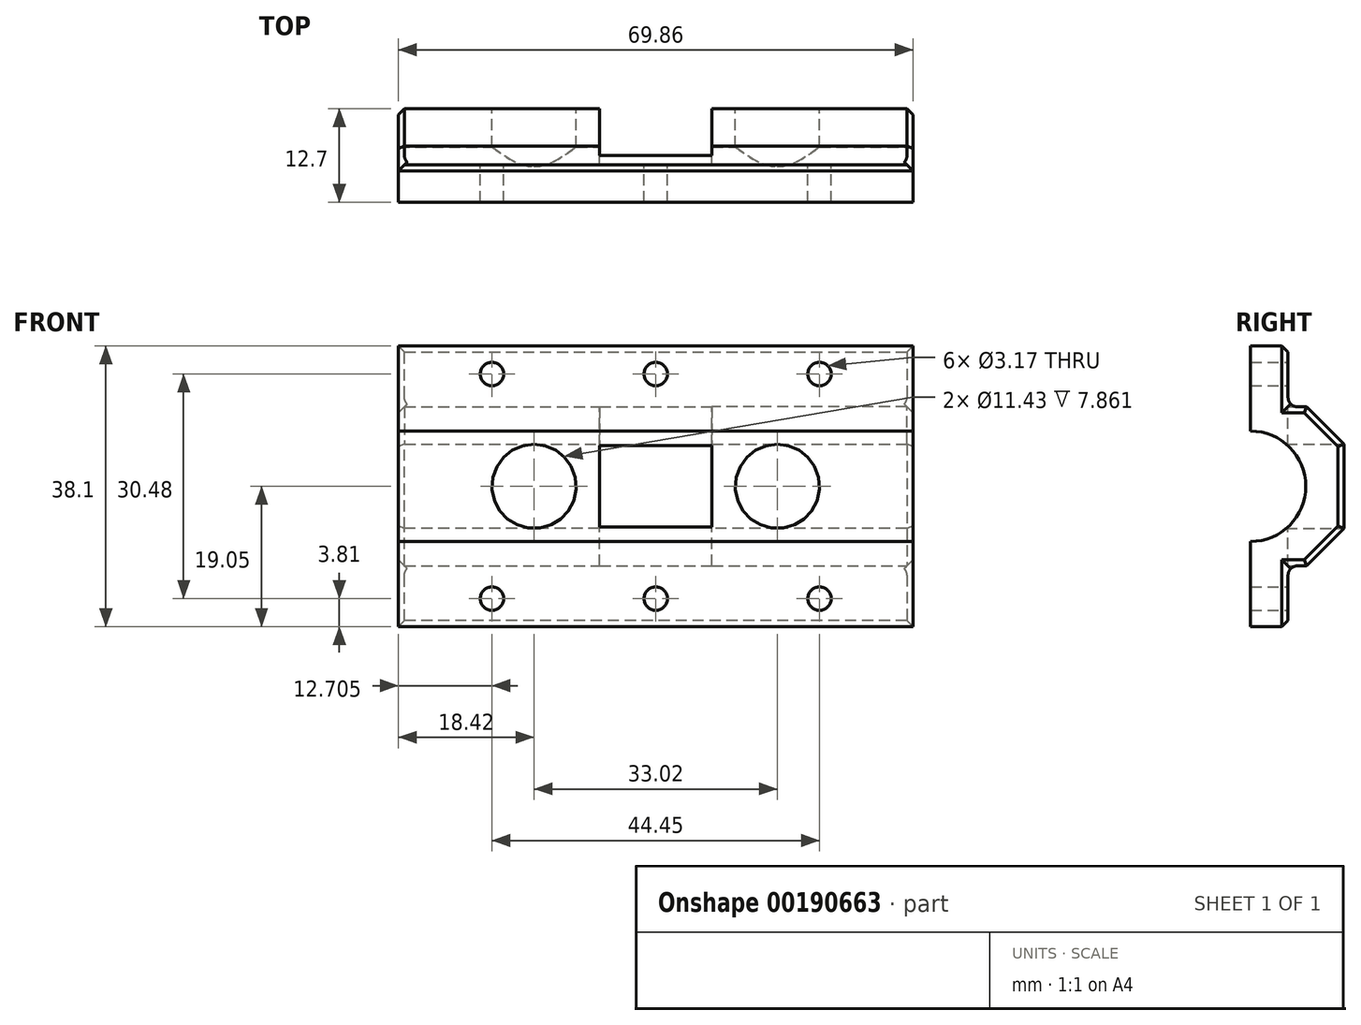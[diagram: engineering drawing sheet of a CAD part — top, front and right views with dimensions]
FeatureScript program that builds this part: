
annotation { "Feature Type Name" : "Feature", "Feature Type Description" : "" }
export const myFeature = defineFeature(function(context is Context, id is Id, definition is map)
    precondition{}
    {
        {
            var Q0;
            Q0=qCreatedBy(makeId("Top.planeOp"),FACE);
            var sketch = newSketch(context, id + "F0", { "sketchPlane" : qUnion([Q0])});
            skLineSegment(sketch, "E0", {"start": v(0, 0) * mm, "end": v(-34.93, 0) * mm});
            skLineSegment(sketch, "E1", {"start": v(-34.93, 0) * mm, "end": v(-34.93, 12.7) * mm});
            skLineSegment(sketch, "E2", {"start": v(-34.93, 12.7) * mm, "end": v(0, 12.7) * mm});
            skLineSegment(sketch, "E3", {"start": v(0, 12.7) * mm, "end": v(0, 0) * mm});
            skLineSegment(sketch, "E4.MirrorCS", {"start": v(34.93, 12.7) * mm, "end": v(0, 12.7) * mm});
            skLineSegment(sketch, "E5.MirrorCS", {"start": v(0, 0) * mm, "end": v(34.93, 0) * mm});
            skLineSegment(sketch, "E6.MirrorCS", {"start": v(34.93, 0) * mm, "end": v(34.93, 12.7) * mm});
            skSolve(sketch);
        }
        {
            var Q0;
            Q0=qSketchRegion(id+"F0",true);
            extrude(context, id + "F1", {"entities" : qUnion([Q0]), "depth" : 10.8 * mm});
        }
        {
            var Q0;
            Q0 = qSketchRegion(id + "F0", true);
            extrude(context, id + "F2", {"entities" : qUnion([Q0]), "operationType" : NewBodyOperationType.ADD, "oppositeDirection" : true, "depth" : 10.8 * mm});
        }
        {
            var Q0;
            Q0=qCreatedBy(makeId("Front.planeOp"),FACE);
            var sketch = newSketch(context, id + "F3", { "sketchPlane" : qUnion([Q0])});
            skLineSegment(sketch, "E7", {"start": v(0, 0) * mm, "end": v(0, 19.05) * mm});
            skLineSegment(sketch, "E8", {"start": v(0, 19.05) * mm, "end": v(-34.93, 19.05) * mm});
            skLineSegment(sketch, "E9", {"start": v(-34.93, 19.05) * mm, "end": v(-34.93, 0) * mm});
            skLineSegment(sketch, "E10", {"start": v(-34.93, 0) * mm, "end": v(0, 0) * mm});
            skLineSegment(sketch, "E11.MirrorCS", {"start": v(0, 19.05) * mm, "end": v(34.93, 19.05) * mm});
            skLineSegment(sketch, "E12.MirrorCS", {"start": v(34.93, 19.05) * mm, "end": v(34.93, 0) * mm});
            skLineSegment(sketch, "E13.MirrorCS", {"start": v(0, -19.05) * mm, "end": v(-34.93, -19.05) * mm});
            skLineSegment(sketch, "E14.MirrorCS", {"start": v(0, -19.05) * mm, "end": v(34.93, -19.05) * mm});
            skLineSegment(sketch, "E15.MirrorCS", {"start": v(-34.93, -19.05) * mm, "end": v(-34.93, 0) * mm});
            skLineSegment(sketch, "E16.MirrorCS", {"start": v(34.93, -19.05) * mm, "end": v(34.93, 0) * mm});
            skLineSegment(sketch, "E17.MirrorCS", {"start": v(0, 0) * mm, "end": v(0, -19.05) * mm});
            skSolve(sketch);
        }
        {
            var Q0;
            Q0 = qSketchRegion(id + "F3", true);
            extrude(context, id + "F4", {"entities" : qUnion([Q0]), "operationType" : NewBodyOperationType.ADD, "oppositeDirection" : true, "depth" : 5.08 * mm});
        }
        {
            var Q0;
            {var subQ0=sQuery(id+"F0.wireOp",EDGE,"E6.MirrorCS");Q0=makeQuery(id+"F4.boolean.opBoolean","MERGE",FACE,{"derivedFrom":[makeQuery(id+"F2.boolean.opBoolean","MERGE",FACE,{"derivedFrom":[makeQuery(id+"F1.opExtrude","SWEPT_FACE",FACE,{"disambiguationData":[OSD([subQ0])]}),makeQuery(id+"F2.opExtrude","SWEPT_FACE",FACE,{"disambiguationData":[OSD([subQ0])]})]}),makeQuery(id+"F4.opExtrude","SWEPT_FACE",FACE,{"disambiguationData":[OSD([sQuery(id+"F3.wireOp",EDGE,"E12.MirrorCS"),sQuery(id+"F3.wireOp",EDGE,"E16.MirrorCS")])]})]});}
            var sketch = newSketch(context, id + "F5", { "sketchPlane" : qUnion([Q0])});
            skCircle(sketch, "E18", {"center": v(0, 0) * mm, "radius": 7.5 * mm});
            skSolve(sketch);
        }
        {
            var Q0;
            Q0 = qSketchRegion(id + "F5", true);
            extrude(context, id + "F6", {"entities" : qUnion([Q0]), "operationType" : NewBodyOperationType.REMOVE, "oppositeDirection" : true, "depth" : 101.6 * mm});
        }
        {
            var Q0;
            {var subQ0=sQuery(id+"F0.wireOp",EDGE,"E4.MirrorCS");var subQ1=sQuery(id+"F0.wireOp",EDGE,"E2");Q0=makeQuery(id+"F2.boolean.opBoolean","MERGE",FACE,{"derivedFrom":[makeQuery(id+"F1.opExtrude","SWEPT_FACE",FACE,{"disambiguationData":[OSD([subQ1,subQ0])]}),makeQuery(id+"F2.opExtrude","SWEPT_FACE",FACE,{"disambiguationData":[OSD([subQ1,subQ0])]})]});}
            var sketch = newSketch(context, id + "F7", { "sketchPlane" : qUnion([Q0])});
            skCircle(sketch, "E19", {"center": v(-22.23, -15.24) * mm, "radius": 1.59 * mm});
            skCircle(sketch, "E20", {"center": v(-22.23, 15.24) * mm, "radius": 1.59 * mm});
            skCircle(sketch, "E21", {"center": v(0, -15.24) * mm, "radius": 1.59 * mm});
            skCircle(sketch, "E22.MirrorC", {"center": v(22.23, 15.24) * mm, "radius": 1.59 * mm});
            skCircle(sketch, "E23.MirrorC", {"center": v(22.23, -15.24) * mm, "radius": 1.59 * mm});
            skCircle(sketch, "E24.MirrorC", {"center": v(0, 15.24) * mm, "radius": 1.59 * mm});
            skSolve(sketch);
        }
        {
            var Q0;
            Q0 = qSketchRegion(id + "F7", true);
            extrude(context, id + "F8", {"entities" : qUnion([Q0]), "operationType" : NewBodyOperationType.REMOVE, "oppositeDirection" : true, "depth" : 25.4 * mm});
        }
        {
            var Q0;
            Q0=makeQuery(id+"F2.opExtrude","CAP_EDGE",EDGE,{"disambiguationData":[OSD([sQuery(id+"F0.wireOp",EDGE,"E2"),sQuery(id+"F0.wireOp",EDGE,"E4.MirrorCS")])],"isStart":false});
            var Q1;
            Q1=makeQuery(id+"F1.opExtrude","CAP_EDGE",EDGE,{"disambiguationData":[OSD([sQuery(id+"F0.wireOp",EDGE,"E2"),sQuery(id+"F0.wireOp",EDGE,"E4.MirrorCS")])],"isStart":false});
            chamfer(context, id + "F9", {"entities" : qUnion([Q0, Q1]), "width" : 5.08 * mm, "tangentPropagation" : true});
        }
        {
            var Q0;
            Q0=makeQuery(id+"F4.opExtrude","CAP_EDGE",EDGE,{"disambiguationData":[OSD([sQuery(id+"F3.wireOp",EDGE,"E13.MirrorCS"),sQuery(id+"F3.wireOp",EDGE,"E14.MirrorCS")])],"isStart":false});
            var Q1;
            {var subQ0=sQuery(id+"F3.wireOp",EDGE,"E15.MirrorCS");var subQ1=sQuery(id+"F3.wireOp",EDGE,"E14.MirrorCS");var subQ2=sQuery(id+"F3.wireOp",EDGE,"E13.MirrorCS");var subQ3=sQuery(id+"F3.wireOp",EDGE,"E9");Q1=makeQuery(id+"F4.boolean.opBoolean","SPLIT",EDGE,{"disambiguationData":[TD([makeQuery(id+"F4.opExtrude","SWEPT_FACE",FACE,{"disambiguationData":[OSD([subQ2,subQ1])]})])],"derivedFrom":makeQuery(id+"F4.opExtrude","CAP_EDGE",EDGE,{"disambiguationData":[OSD([subQ3,subQ0])],"isStart":false})});}
            var Q2;
            {var subQ0=sQuery(id+"F0.wireOp",EDGE,"E1");Q2=makeQuery(id+"F9.opChamfer","BLEND_EDGE",EDGE,{"blendedFrom":[makeQuery(id+"F1.opExtrude","CAP_EDGE",EDGE,{"disambiguationData":[OSD([sQuery(id+"F0.wireOp",EDGE,"E2"),sQuery(id+"F0.wireOp",EDGE,"E4.MirrorCS")])],"isStart":false}),makeQuery(id+"F4.boolean.opBoolean","MERGE",FACE,{"derivedFrom":[makeQuery(id+"F2.boolean.opBoolean","MERGE",FACE,{"derivedFrom":[makeQuery(id+"F1.opExtrude","SWEPT_FACE",FACE,{"disambiguationData":[OSD([subQ0])]}),makeQuery(id+"F2.opExtrude","SWEPT_FACE",FACE,{"disambiguationData":[OSD([subQ0])]})]}),makeQuery(id+"F4.opExtrude","SWEPT_FACE",FACE,{"disambiguationData":[OSD([sQuery(id+"F3.wireOp",EDGE,"E9"),sQuery(id+"F3.wireOp",EDGE,"E15.MirrorCS")])]})]})],"blendedInto":[makeQuery(id+"F4.boolean.opBoolean","MERGE",FACE,{"derivedFrom":[makeQuery(id+"F2.boolean.opBoolean","MERGE",FACE,{"derivedFrom":[makeQuery(id+"F1.opExtrude","SWEPT_FACE",FACE,{"disambiguationData":[OSD([subQ0])]}),makeQuery(id+"F2.opExtrude","SWEPT_FACE",FACE,{"disambiguationData":[OSD([subQ0])]})]}),makeQuery(id+"F4.opExtrude","SWEPT_FACE",FACE,{"disambiguationData":[OSD([sQuery(id+"F3.wireOp",EDGE,"E9"),sQuery(id+"F3.wireOp",EDGE,"E15.MirrorCS")])]})]})]});}
            var Q3;
            {var subQ0=sQuery(id+"F0.wireOp",EDGE,"E2");var subQ1=sQuery(id+"F0.wireOp",EDGE,"E1");Q3=makeQuery(id+"F2.boolean.opBoolean","MERGE",EDGE,{"derivedFrom":[makeQuery(id+"F1.opExtrude","SWEPT_EDGE",EDGE,{"disambiguationData":[OSD([subQ1,subQ0])]}),makeQuery(id+"F2.opExtrude","SWEPT_EDGE",EDGE,{"disambiguationData":[OSD([subQ1,subQ0])]})]});}
            var Q4;
            {var subQ0=sQuery(id+"F0.wireOp",EDGE,"E1");Q4=makeQuery(id+"F9.opChamfer","BLEND_EDGE",EDGE,{"blendedFrom":[makeQuery(id+"F2.opExtrude","CAP_EDGE",EDGE,{"disambiguationData":[OSD([sQuery(id+"F0.wireOp",EDGE,"E2"),sQuery(id+"F0.wireOp",EDGE,"E4.MirrorCS")])],"isStart":false}),makeQuery(id+"F4.boolean.opBoolean","MERGE",FACE,{"derivedFrom":[makeQuery(id+"F2.boolean.opBoolean","MERGE",FACE,{"derivedFrom":[makeQuery(id+"F1.opExtrude","SWEPT_FACE",FACE,{"disambiguationData":[OSD([subQ0])]}),makeQuery(id+"F2.opExtrude","SWEPT_FACE",FACE,{"disambiguationData":[OSD([subQ0])]})]}),makeQuery(id+"F4.opExtrude","SWEPT_FACE",FACE,{"disambiguationData":[OSD([sQuery(id+"F3.wireOp",EDGE,"E9"),sQuery(id+"F3.wireOp",EDGE,"E15.MirrorCS")])]})]})],"blendedInto":[makeQuery(id+"F4.boolean.opBoolean","MERGE",FACE,{"derivedFrom":[makeQuery(id+"F2.boolean.opBoolean","MERGE",FACE,{"derivedFrom":[makeQuery(id+"F1.opExtrude","SWEPT_FACE",FACE,{"disambiguationData":[OSD([subQ0])]}),makeQuery(id+"F2.opExtrude","SWEPT_FACE",FACE,{"disambiguationData":[OSD([subQ0])]})]}),makeQuery(id+"F4.opExtrude","SWEPT_FACE",FACE,{"disambiguationData":[OSD([sQuery(id+"F3.wireOp",EDGE,"E9"),sQuery(id+"F3.wireOp",EDGE,"E15.MirrorCS")])]})]})]});}
            var Q5;
            {var subQ0=sQuery(id+"F0.wireOp",EDGE,"E6.MirrorCS");Q5=makeQuery(id+"F9.opChamfer","BLEND_EDGE",EDGE,{"blendedFrom":[makeQuery(id+"F1.opExtrude","CAP_EDGE",EDGE,{"disambiguationData":[OSD([sQuery(id+"F0.wireOp",EDGE,"E2"),sQuery(id+"F0.wireOp",EDGE,"E4.MirrorCS")])],"isStart":false}),makeQuery(id+"F4.boolean.opBoolean","MERGE",FACE,{"derivedFrom":[makeQuery(id+"F2.boolean.opBoolean","MERGE",FACE,{"derivedFrom":[makeQuery(id+"F1.opExtrude","SWEPT_FACE",FACE,{"disambiguationData":[OSD([subQ0])]}),makeQuery(id+"F2.opExtrude","SWEPT_FACE",FACE,{"disambiguationData":[OSD([subQ0])]})]}),makeQuery(id+"F4.opExtrude","SWEPT_FACE",FACE,{"disambiguationData":[OSD([sQuery(id+"F3.wireOp",EDGE,"E12.MirrorCS"),sQuery(id+"F3.wireOp",EDGE,"E16.MirrorCS")])]})]})],"blendedInto":[makeQuery(id+"F4.boolean.opBoolean","MERGE",FACE,{"derivedFrom":[makeQuery(id+"F2.boolean.opBoolean","MERGE",FACE,{"derivedFrom":[makeQuery(id+"F1.opExtrude","SWEPT_FACE",FACE,{"disambiguationData":[OSD([subQ0])]}),makeQuery(id+"F2.opExtrude","SWEPT_FACE",FACE,{"disambiguationData":[OSD([subQ0])]})]}),makeQuery(id+"F4.opExtrude","SWEPT_FACE",FACE,{"disambiguationData":[OSD([sQuery(id+"F3.wireOp",EDGE,"E12.MirrorCS"),sQuery(id+"F3.wireOp",EDGE,"E16.MirrorCS")])]})]})]});}
            var Q6;
            {var subQ0=sQuery(id+"F0.wireOp",EDGE,"E6.MirrorCS");var subQ1=sQuery(id+"F0.wireOp",EDGE,"E4.MirrorCS");Q6=makeQuery(id+"F2.boolean.opBoolean","MERGE",EDGE,{"derivedFrom":[makeQuery(id+"F1.opExtrude","SWEPT_EDGE",EDGE,{"disambiguationData":[OSD([subQ1,subQ0])]}),makeQuery(id+"F2.opExtrude","SWEPT_EDGE",EDGE,{"disambiguationData":[OSD([subQ1,subQ0])]})]});}
            var Q7;
            {var subQ0=sQuery(id+"F0.wireOp",EDGE,"E6.MirrorCS");Q7=makeQuery(id+"F9.opChamfer","BLEND_EDGE",EDGE,{"blendedFrom":[makeQuery(id+"F2.opExtrude","CAP_EDGE",EDGE,{"disambiguationData":[OSD([sQuery(id+"F0.wireOp",EDGE,"E2"),sQuery(id+"F0.wireOp",EDGE,"E4.MirrorCS")])],"isStart":false}),makeQuery(id+"F4.boolean.opBoolean","MERGE",FACE,{"derivedFrom":[makeQuery(id+"F2.boolean.opBoolean","MERGE",FACE,{"derivedFrom":[makeQuery(id+"F1.opExtrude","SWEPT_FACE",FACE,{"disambiguationData":[OSD([subQ0])]}),makeQuery(id+"F2.opExtrude","SWEPT_FACE",FACE,{"disambiguationData":[OSD([subQ0])]})]}),makeQuery(id+"F4.opExtrude","SWEPT_FACE",FACE,{"disambiguationData":[OSD([sQuery(id+"F3.wireOp",EDGE,"E12.MirrorCS"),sQuery(id+"F3.wireOp",EDGE,"E16.MirrorCS")])]})]})],"blendedInto":[makeQuery(id+"F4.boolean.opBoolean","MERGE",FACE,{"derivedFrom":[makeQuery(id+"F2.boolean.opBoolean","MERGE",FACE,{"derivedFrom":[makeQuery(id+"F1.opExtrude","SWEPT_FACE",FACE,{"disambiguationData":[OSD([subQ0])]}),makeQuery(id+"F2.opExtrude","SWEPT_FACE",FACE,{"disambiguationData":[OSD([subQ0])]})]}),makeQuery(id+"F4.opExtrude","SWEPT_FACE",FACE,{"disambiguationData":[OSD([sQuery(id+"F3.wireOp",EDGE,"E12.MirrorCS"),sQuery(id+"F3.wireOp",EDGE,"E16.MirrorCS")])]})]})]});}
            var Q8;
            Q8=makeQuery(id+"F2.opExtrude","CAP_EDGE",EDGE,{"disambiguationData":[OSD([sQuery(id+"F0.wireOp",EDGE,"E6.MirrorCS")])],"isStart":false});
            var Q9;
            {var subQ0=sQuery(id+"F3.wireOp",EDGE,"E16.MirrorCS");var subQ1=sQuery(id+"F3.wireOp",EDGE,"E14.MirrorCS");var subQ2=sQuery(id+"F3.wireOp",EDGE,"E13.MirrorCS");var subQ3=sQuery(id+"F3.wireOp",EDGE,"E12.MirrorCS");Q9=makeQuery(id+"F4.boolean.opBoolean","SPLIT",EDGE,{"disambiguationData":[TD([makeQuery(id+"F4.opExtrude","SWEPT_FACE",FACE,{"disambiguationData":[OSD([subQ2,subQ1])]})])],"derivedFrom":makeQuery(id+"F4.opExtrude","CAP_EDGE",EDGE,{"disambiguationData":[OSD([subQ3,subQ0])],"isStart":false})});}
            var Q10;
            Q10=makeQuery(id+"F4.opExtrude","CAP_EDGE",EDGE,{"disambiguationData":[OSD([sQuery(id+"F3.wireOp",EDGE,"E8"),sQuery(id+"F3.wireOp",EDGE,"E11.MirrorCS")])],"isStart":false});
            var Q11;
            {var subQ0=sQuery(id+"F3.wireOp",EDGE,"E15.MirrorCS");var subQ1=sQuery(id+"F3.wireOp",EDGE,"E11.MirrorCS");var subQ2=sQuery(id+"F3.wireOp",EDGE,"E9");var subQ3=sQuery(id+"F3.wireOp",EDGE,"E8");Q11=makeQuery(id+"F4.boolean.opBoolean","SPLIT",EDGE,{"disambiguationData":[TD([makeQuery(id+"F4.opExtrude","SWEPT_FACE",FACE,{"disambiguationData":[OSD([subQ3,subQ1])]})])],"derivedFrom":makeQuery(id+"F4.opExtrude","CAP_EDGE",EDGE,{"disambiguationData":[OSD([subQ2,subQ0])],"isStart":false})});}
            var Q12;
            Q12=makeQuery(id+"F1.opExtrude","CAP_EDGE",EDGE,{"disambiguationData":[OSD([sQuery(id+"F0.wireOp",EDGE,"E1")])],"isStart":false});
            var Q13;
            {var subQ0=sQuery(id+"F3.wireOp",EDGE,"E16.MirrorCS");var subQ1=sQuery(id+"F3.wireOp",EDGE,"E12.MirrorCS");var subQ2=sQuery(id+"F3.wireOp",EDGE,"E11.MirrorCS");var subQ3=sQuery(id+"F3.wireOp",EDGE,"E8");Q13=makeQuery(id+"F4.boolean.opBoolean","SPLIT",EDGE,{"disambiguationData":[TD([makeQuery(id+"F4.opExtrude","SWEPT_FACE",FACE,{"disambiguationData":[OSD([subQ3,subQ2])]})])],"derivedFrom":makeQuery(id+"F4.opExtrude","CAP_EDGE",EDGE,{"disambiguationData":[OSD([subQ1,subQ0])],"isStart":false})});}
            var Q14;
            Q14=makeQuery(id+"F1.opExtrude","CAP_EDGE",EDGE,{"disambiguationData":[OSD([sQuery(id+"F0.wireOp",EDGE,"E6.MirrorCS")])],"isStart":false});
            var Q15;
            Q15=makeQuery(id+"F2.opExtrude","CAP_EDGE",EDGE,{"disambiguationData":[OSD([sQuery(id+"F0.wireOp",EDGE,"E1")])],"isStart":false});
            chamfer(context, id + "F10", {"entities" : qUnion([Q0, Q1, Q2, Q3, Q4, Q5, Q6, Q7, Q8, Q9, Q10, Q11, Q12, Q13, Q14, Q15]), "width" : 0.83 * mm, "tangentPropagation" : true});
        }
        {
            var Q0;
            Q0=makeQuery(id+"F4.boolean.opBoolean","INTERSECT",EDGE,{"derivedFrom":[makeQuery(id+"F2.opExtrude","CAP_FACE",FACE,{"disambiguationData":[OSD([sQuery(id+"F0.wireOp",EDGE,"E0"),sQuery(id+"F0.wireOp",EDGE,"E1"),sQuery(id+"F0.wireOp",EDGE,"E2"),sQuery(id+"F0.wireOp",EDGE,"E4.MirrorCS"),sQuery(id+"F0.wireOp",EDGE,"E5.MirrorCS"),sQuery(id+"F0.wireOp",EDGE,"E6.MirrorCS")])],"isStart":false}),makeQuery(id+"F4.opExtrude","CAP_FACE",FACE,{"disambiguationData":[OSD([sQuery(id+"F3.wireOp",EDGE,"E8"),sQuery(id+"F3.wireOp",EDGE,"E9"),sQuery(id+"F3.wireOp",EDGE,"E11.MirrorCS"),sQuery(id+"F3.wireOp",EDGE,"E12.MirrorCS"),sQuery(id+"F3.wireOp",EDGE,"E13.MirrorCS"),sQuery(id+"F3.wireOp",EDGE,"E14.MirrorCS"),sQuery(id+"F3.wireOp",EDGE,"E15.MirrorCS"),sQuery(id+"F3.wireOp",EDGE,"E16.MirrorCS")])],"isStart":false})]});
            var Q1;
            {var subQ0=sQuery(id+"F0.wireOp",EDGE,"E1");var subQ1=sQuery(id+"F0.wireOp",EDGE,"E6.MirrorCS");var subQ2=makeQuery(id+"F1.opExtrude","CAP_FACE",FACE,{"disambiguationData":[OSD([sQuery(id+"F0.wireOp",EDGE,"E0"),subQ0,sQuery(id+"F0.wireOp",EDGE,"E2"),sQuery(id+"F0.wireOp",EDGE,"E4.MirrorCS"),sQuery(id+"F0.wireOp",EDGE,"E5.MirrorCS"),subQ1])],"isStart":false});var subQ3=sQuery(id+"F3.wireOp",EDGE,"E11.MirrorCS");var subQ4=sQuery(id+"F3.wireOp",EDGE,"E8");var subQ5=sQuery(id+"F3.wireOp",EDGE,"E15.MirrorCS");var subQ6=sQuery(id+"F3.wireOp",EDGE,"E9");var subQ7=sQuery(id+"F3.wireOp",EDGE,"E16.MirrorCS");var subQ8=sQuery(id+"F3.wireOp",EDGE,"E12.MirrorCS");var subQ9=makeQuery(id+"F4.opExtrude","CAP_FACE",FACE,{"disambiguationData":[OSD([subQ4,subQ6,subQ3,subQ8,sQuery(id+"F3.wireOp",EDGE,"E13.MirrorCS"),sQuery(id+"F3.wireOp",EDGE,"E14.MirrorCS"),subQ5,subQ7])],"isStart":false});Q1=makeQuery(id+"F10.opChamfer","BLEND_EDGE",EDGE,{"blendedFrom":[makeQuery(id+"F4.boolean.opBoolean","INTERSECT",EDGE,{"derivedFrom":[subQ2,subQ9]}),makeQuery(id+"F4.boolean.opBoolean","SPLIT",FACE,{"disambiguationData":[TD([makeQuery(id+"F4.opExtrude","SWEPT_FACE",FACE,{"disambiguationData":[OSD([subQ4,subQ3])]})])],"derivedFrom":subQ9})],"blendedInto":[makeQuery(id+"F4.boolean.opBoolean","SPLIT",FACE,{"disambiguationData":[TD([makeQuery(id+"F4.opExtrude","SWEPT_FACE",FACE,{"disambiguationData":[OSD([subQ4,subQ3])]})])],"derivedFrom":subQ9})]});}
            var Q2;
            Q2=makeQuery(id+"F4.boolean.opBoolean","INTERSECT",EDGE,{"derivedFrom":[makeQuery(id+"F1.opExtrude","CAP_FACE",FACE,{"disambiguationData":[OSD([sQuery(id+"F0.wireOp",EDGE,"E0"),sQuery(id+"F0.wireOp",EDGE,"E1"),sQuery(id+"F0.wireOp",EDGE,"E2"),sQuery(id+"F0.wireOp",EDGE,"E4.MirrorCS"),sQuery(id+"F0.wireOp",EDGE,"E5.MirrorCS"),sQuery(id+"F0.wireOp",EDGE,"E6.MirrorCS")])],"isStart":false}),makeQuery(id+"F4.opExtrude","CAP_FACE",FACE,{"disambiguationData":[OSD([sQuery(id+"F3.wireOp",EDGE,"E8"),sQuery(id+"F3.wireOp",EDGE,"E9"),sQuery(id+"F3.wireOp",EDGE,"E11.MirrorCS"),sQuery(id+"F3.wireOp",EDGE,"E12.MirrorCS"),sQuery(id+"F3.wireOp",EDGE,"E13.MirrorCS"),sQuery(id+"F3.wireOp",EDGE,"E14.MirrorCS"),sQuery(id+"F3.wireOp",EDGE,"E15.MirrorCS"),sQuery(id+"F3.wireOp",EDGE,"E16.MirrorCS")])],"isStart":false})]});
            fillet(context, id + "F11", {"entities" : qUnion([Q0, Q1, Q2]), "radius" : 1.27 * mm, "tangentPropagation" : true, "allowEdgeOverflow" : false});
        }
        {
            var Q0;
            {var subQ0=sQuery(id+"F0.wireOp",EDGE,"E4.MirrorCS");var subQ1=sQuery(id+"F0.wireOp",EDGE,"E2");Q0=makeQuery(id+"F2.boolean.opBoolean","MERGE",FACE,{"derivedFrom":[makeQuery(id+"F1.opExtrude","SWEPT_FACE",FACE,{"disambiguationData":[OSD([subQ1,subQ0])]}),makeQuery(id+"F2.opExtrude","SWEPT_FACE",FACE,{"disambiguationData":[OSD([subQ1,subQ0])]})]});}
            var sketch = newSketch(context, id + "F12", { "sketchPlane" : qUnion([Q0])});
            skCircle(sketch, "E25", {"center": v(-16.51, 0) * mm, "radius": 5.72 * mm});
            skCircle(sketch, "E26.MirrorC", {"center": v(16.51, 0) * mm, "radius": 5.72 * mm});
            skSolve(sketch);
        }
        {
            var Q0;
            Q0 = qSketchRegion(id + "F12", true);
            extrude(context, id + "F13", {"entities" : qUnion([Q0]), "operationType" : NewBodyOperationType.REMOVE, "oppositeDirection" : true, "depth" : 25.4 * mm});
        }
        {
            var Q0;
            {var subQ0=sQuery(id+"F0.wireOp",EDGE,"E4.MirrorCS");var subQ1=sQuery(id+"F0.wireOp",EDGE,"E2");var subQ2=makeQuery(id+"F2.opExtrude","SWEPT_FACE",FACE,{"disambiguationData":[OSD([subQ1,subQ0])]});var subQ3=makeQuery(id+"F1.opExtrude","SWEPT_FACE",FACE,{"disambiguationData":[OSD([subQ1,subQ0])]});Q0=makeQuery(id+"F13.boolean.opBoolean","SPLIT",FACE,{"disambiguationData":[TD([subQ3,subQ2,makeQuery(id+"F9.opChamfer","BLEND_FACE",FACE,{"disambiguationData":[OSD([subQ1,subQ0]),TDD([makeQuery(id+"F1.opExtrude","CAP_EDGE",EDGE,{"disambiguationData":[OSD([subQ1,subQ0])],"isStart":false})])]}),makeQuery(id+"F9.opChamfer","BLEND_FACE",FACE,{"disambiguationData":[OSD([subQ1,subQ0]),TDD([makeQuery(id+"F2.opExtrude","CAP_EDGE",EDGE,{"disambiguationData":[OSD([subQ1,subQ0])],"isStart":false})])]}),makeQuery(id+"F13.opExtrude","SWEPT_FACE",FACE,{"disambiguationData":[OSD([sQuery(id+"F12.wireOp",EDGE,"E25")])]}),makeQuery(id+"F13.opExtrude","SWEPT_FACE",FACE,{"disambiguationData":[OSD([sQuery(id+"F12.wireOp",EDGE,"E26.MirrorC")])]})])],"derivedFrom":makeQuery(id+"F2.boolean.opBoolean","MERGE",FACE,{"derivedFrom":[subQ3,subQ2]})});}
            var sketch = newSketch(context, id + "F14", { "sketchPlane" : qUnion([Q0])});
            skLineSegment(sketch, "E27", {"start": v(0, 0) * mm, "end": v(0, 5.71) * mm});
            skLineSegment(sketch, "E28", {"start": v(0, 5.71) * mm, "end": v(-7.62, 5.71) * mm});
            skLineSegment(sketch, "E29", {"start": v(-7.62, 5.71) * mm, "end": v(-7.62, -5.71) * mm});
            skLineSegment(sketch, "E30", {"start": v(-7.62, -5.71) * mm, "end": v(0, -5.71) * mm});
            skLineSegment(sketch, "E31", {"start": v(0, -5.71) * mm, "end": v(0, 0) * mm});
            skLineSegment(sketch, "E32.MirrorCS", {"start": v(0, 5.71) * mm, "end": v(7.62, 5.71) * mm});
            skLineSegment(sketch, "E33.MirrorCS", {"start": v(7.62, 5.71) * mm, "end": v(7.62, -5.71) * mm});
            skLineSegment(sketch, "E34.MirrorCS", {"start": v(7.62, -5.71) * mm, "end": v(0, -5.71) * mm});
            skLineSegment(sketch, "E35", {"start": v(-7.62, 5.71) * mm, "end": v(-7.62, 10.8) * mm});
            skLineSegment(sketch, "E36", {"start": v(-7.62, 10.8) * mm, "end": v(0, 10.8) * mm});
            skLineSegment(sketch, "E37", {"start": v(0, 10.8) * mm, "end": v(0, 5.71) * mm});
            skLineSegment(sketch, "E38.MirrorCS", {"start": v(0, -10.8) * mm, "end": v(0, -5.71) * mm});
            skLineSegment(sketch, "E39.MirrorCS", {"start": v(-7.62, -10.8) * mm, "end": v(0, -10.8) * mm});
            skLineSegment(sketch, "E40.MirrorCS", {"start": v(-7.62, -5.71) * mm, "end": v(-7.62, -10.8) * mm});
            skLineSegment(sketch, "E41.MirrorCS", {"start": v(7.62, 10.8) * mm, "end": v(0, 10.8) * mm});
            skLineSegment(sketch, "E42.MirrorCS", {"start": v(7.62, 5.71) * mm, "end": v(7.62, 10.8) * mm});
            skLineSegment(sketch, "E43.MirrorCS", {"start": v(7.62, -5.71) * mm, "end": v(7.62, -10.8) * mm});
            skLineSegment(sketch, "E44.MirrorCS", {"start": v(7.62, -10.8) * mm, "end": v(0, -10.8) * mm});
            skSolve(sketch);
        }
        {
            var Q0;
            Q0 = qSketchRegion(id + "F14", true);
            extrude(context, id + "F15", {"entities" : qUnion([Q0]), "operationType" : NewBodyOperationType.REMOVE, "oppositeDirection" : true, "depth" : 7.62 * mm});
        }
    });
